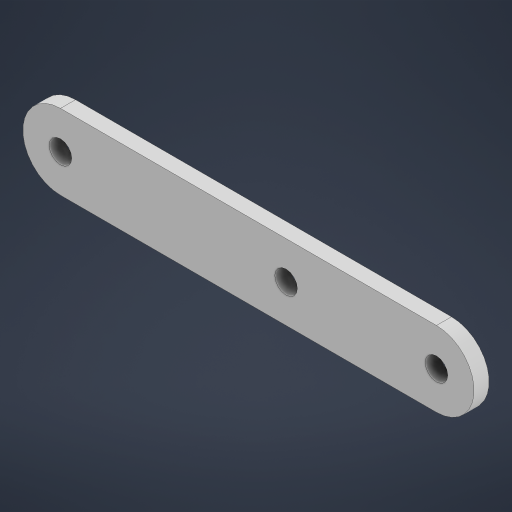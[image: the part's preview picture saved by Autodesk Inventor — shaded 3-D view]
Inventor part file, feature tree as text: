
AUTODESK INVENTOR PART (.ipt)
format: ipt  version: 2023 (Build 270158000, 158)  size: 184,832 bytes
history: native  units: mm
features: extrude x2, sketch x2, fillet x1
ambient origin geometry x8: Origin, YZ Plane, XZ Plane, XY Plane, X Axis, Y Axis, Z Axis, Center Point
bodies: Solid1 (feature_tree)
feature tree (5):
  extrude  "Extrusion1"  Depth=10.0mm
  fillet  "Fillet1"  Radius=2.0mm
  extrude  "Extrusion2"  Depth=5.0mm
  sketch  "Sketch1"  dims[d0=60.0mm d1=10.0mm d2=2.0mm d3=0.0mm]
  sketch  "Sketch2"  dims[d4=5.0mm d5=3.0mm d6=3.0mm d7=2.0mm d8=0.0mm d9=5.0mm d10=3.0mm]
